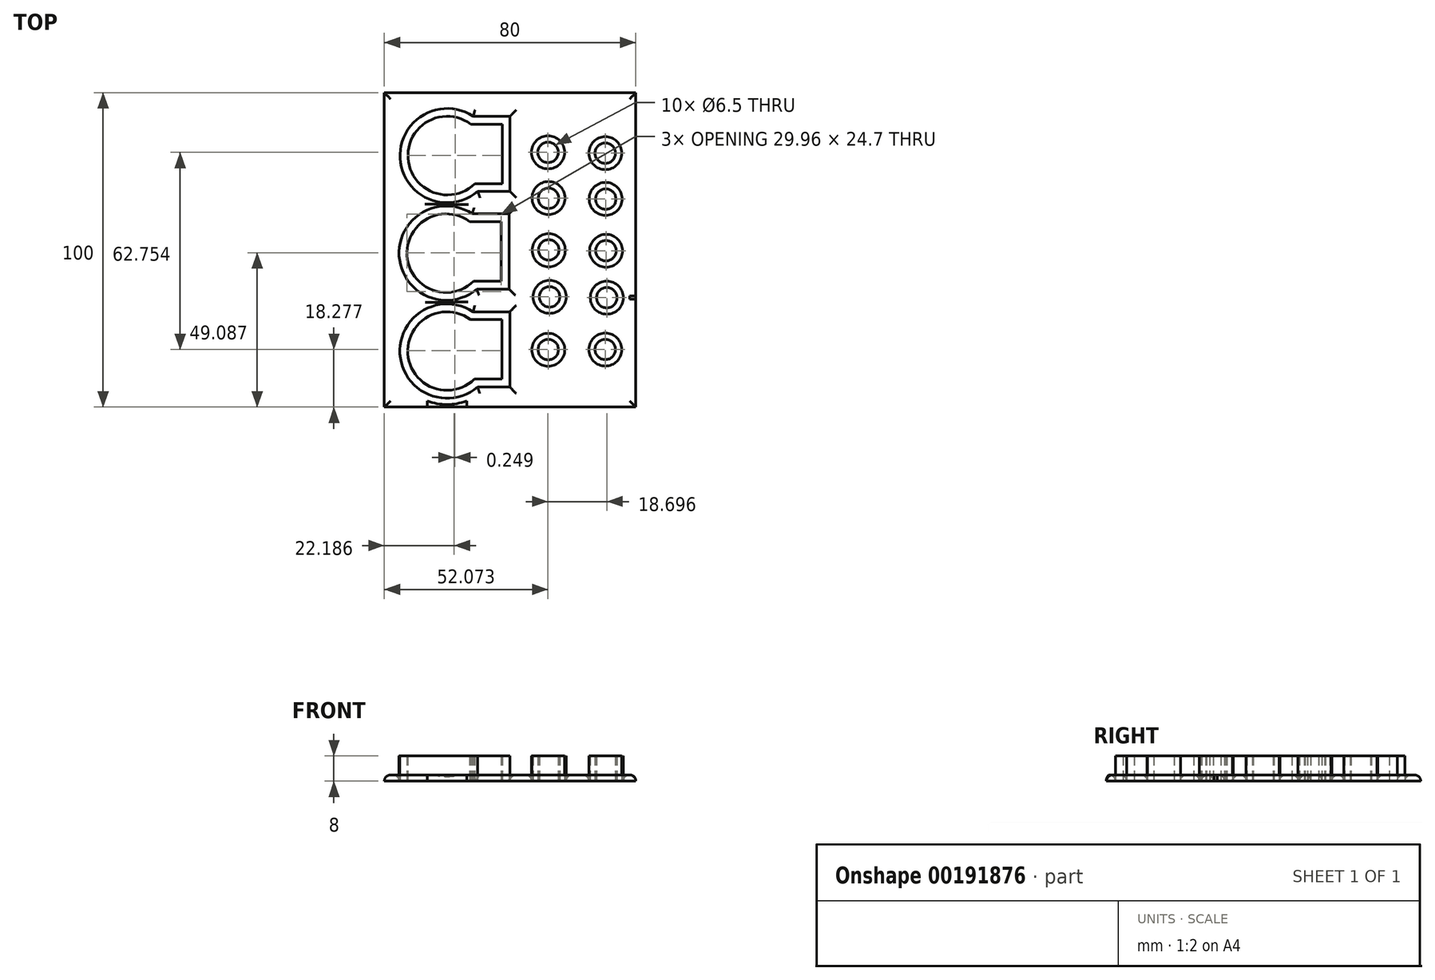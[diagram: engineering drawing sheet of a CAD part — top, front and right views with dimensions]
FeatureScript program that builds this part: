
annotation { "Feature Type Name" : "Feature", "Feature Type Description" : "" }
export const myFeature = defineFeature(function(context is Context, id is Id, definition is map)
    precondition{}
    {
        {
            var Q0;
            Q0=qCreatedBy(makeId("Top.planeOp"),FACE);
            var sketch = newSketch(context, id + "F0", { "sketchPlane" : qUnion([Q0])});
            skLineSegment(sketch, "E0.bottom", {"start": v(40, -50) * mm, "end": v(-40, -50) * mm});
            skLineSegment(sketch, "E0.top", {"start": v(40, 50) * mm, "end": v(-40, 50) * mm});
            skLineSegment(sketch, "E0.left", {"start": v(40, -50) * mm, "end": v(40, 50) * mm});
            skLineSegment(sketch, "E0.right", {"start": v(-40, -50) * mm, "end": v(-40, 50) * mm});
            skPoint(sketch, "E0.middle", {"position": v(0, 0) * mm});
            skArc(sketch, "E1", {"start": v(-12.51, 40) * mm, "mid": v(-32.47, 29.17) * mm, "end": v(-11.25, 21.07) * mm});
            skLineSegment(sketch, "E2.bottom", {"start": v(-2.51, 21.07) * mm, "end": v(-11.25, 21.07) * mm});
            skLineSegment(sketch, "E2.top", {"start": v(-2.51, 40) * mm, "end": v(-12.51, 40) * mm});
            skLineSegment(sketch, "E2.left", {"start": v(-2.51, 21.07) * mm, "end": v(-2.51, 40) * mm});
            skPoint(sketch, "E2.middle", {"position": v(-7.51, 30.54) * mm});
            skLineSegment(sketch, "E3.trimOffspring", {"start": v(-12.51, 40) * mm, "end": v(-12.51, 40) * mm});
            skPoint(sketch, "E4.orphan", {"position": v(-40, 25) * mm});
            skPoint(sketch, "E5.middle", {"position": v(-7.56, -0.43) * mm});
            skPoint(sketch, "E6.middle", {"position": v(0.3, -31.2) * mm});
            skPoint(sketch, "E7.middle", {"position": v(-7.26, -31.66) * mm});
            skCircle(sketch, "E8", {"center": v(12.29, 0) * mm, "radius": 3.25 * mm});
            skCircle(sketch, "E9", {"center": v(30.5, -0.27) * mm, "radius": 3.25 * mm});
            skCircle(sketch, "E10", {"center": v(12.23, 16.42) * mm, "radius": 3.25 * mm});
            skCircle(sketch, "E11", {"center": v(30.43, 16.15) * mm, "radius": 3.25 * mm});
            skCircle(sketch, "E12", {"center": v(12.07, 31.03) * mm, "radius": 3.25 * mm});
            skCircle(sketch, "E13", {"center": v(30.28, 30.76) * mm, "radius": 3.25 * mm});
            skCircle(sketch, "E14", {"center": v(12.57, -14.93) * mm, "radius": 3.25 * mm});
            skCircle(sketch, "E15", {"center": v(30.77, -15.2) * mm, "radius": 3.25 * mm});
            skCircle(sketch, "E16", {"center": v(12.14, -31.72) * mm, "radius": 3.25 * mm});
            skCircle(sketch, "E17", {"center": v(30.29, -31.67) * mm, "radius": 3.25 * mm});
            skPoint(sketch, "E18.orphan", {"position": v(-12.51, 21.07) * mm});
            skPoint(sketch, "E19.orphan", {"position": v(-12.56, -10.43) * mm});
            skPoint(sketch, "E20.orphan", {"position": v(-12.26, -41.66) * mm});
            skArc(sketch, "E21.0", {"start": v(-11.72, 42.5) * mm, "mid": v(-34.97, 29.1) * mm, "end": v(-10.28, 18.57) * mm});
            skLineSegment(sketch, "E21.1", {"start": v(-0.01, 42.5) * mm, "end": v(-11.72, 42.5) * mm});
            skLineSegment(sketch, "E21.2", {"start": v(-0.01, 18.57) * mm, "end": v(-0.01, 42.5) * mm});
            skLineSegment(sketch, "E21.3", {"start": v(-0.01, 18.57) * mm, "end": v(-10.28, 18.57) * mm});
            skArc(sketch, "E22", {"start": v(-12.83, 8.98) * mm, "mid": v(-32.8, -1.86) * mm, "end": v(-11.57, -9.96) * mm});
            skLineSegment(sketch, "E23.bottom", {"start": v(-2.83, -9.96) * mm, "end": v(-11.57, -9.96) * mm});
            skLineSegment(sketch, "E23.top", {"start": v(-2.83, 8.98) * mm, "end": v(-12.83, 8.98) * mm});
            skLineSegment(sketch, "E23.left", {"start": v(-2.83, -9.96) * mm, "end": v(-2.83, 8.98) * mm});
            skPoint(sketch, "E23.middle", {"position": v(-7.83, -0.49) * mm});
            skLineSegment(sketch, "E24.trimOffspring", {"start": v(-12.83, 8.98) * mm, "end": v(-12.83, 8.98) * mm});
            skPoint(sketch, "E25.orphan", {"position": v(-12.83, -9.96) * mm});
            skArc(sketch, "E26.0", {"start": v(-12.04, 11.48) * mm, "mid": v(-35.3, -1.93) * mm, "end": v(-10.6, -12.46) * mm});
            skLineSegment(sketch, "E26.1", {"start": v(-0.33, 11.48) * mm, "end": v(-12.04, 11.48) * mm});
            skLineSegment(sketch, "E26.2", {"start": v(-0.33, -12.46) * mm, "end": v(-0.33, 11.48) * mm});
            skLineSegment(sketch, "E26.3", {"start": v(-0.33, -12.46) * mm, "end": v(-10.6, -12.46) * mm});
            skArc(sketch, "E27", {"start": v(-12.58, -22.18) * mm, "mid": v(-32.55, -33.02) * mm, "end": v(-11.32, -41.11) * mm});
            skLineSegment(sketch, "E28.bottom", {"start": v(-2.58, -41.11) * mm, "end": v(-11.32, -41.11) * mm});
            skLineSegment(sketch, "E28.top", {"start": v(-2.58, -22.18) * mm, "end": v(-12.58, -22.18) * mm});
            skLineSegment(sketch, "E28.left", {"start": v(-2.58, -41.11) * mm, "end": v(-2.58, -22.18) * mm});
            skPoint(sketch, "E28.middle", {"position": v(-7.58, -31.65) * mm});
            skLineSegment(sketch, "E29.trimOffspring", {"start": v(-12.58, -22.18) * mm, "end": v(-12.58, -22.18) * mm});
            skPoint(sketch, "E30.orphan", {"position": v(-12.58, -41.11) * mm});
            skArc(sketch, "E31.0", {"start": v(-11.8, -19.68) * mm, "mid": v(-35.05, -33.09) * mm, "end": v(-10.36, -43.61) * mm});
            skLineSegment(sketch, "E31.1", {"start": v(-0.08, -19.68) * mm, "end": v(-11.8, -19.68) * mm});
            skLineSegment(sketch, "E31.2", {"start": v(-0.08, -43.61) * mm, "end": v(-0.08, -19.68) * mm});
            skLineSegment(sketch, "E31.3", {"start": v(-0.08, -43.61) * mm, "end": v(-10.36, -43.61) * mm});
            skCircle(sketch, "E32.0", {"center": v(12.07, 31.03) * mm, "radius": 5.25 * mm});
            skCircle(sketch, "E33.0", {"center": v(30.3, 30.78) * mm, "radius": 5.25 * mm});
            skCircle(sketch, "E34.0", {"center": v(30.4, 16.22) * mm, "radius": 5.25 * mm});
            skCircle(sketch, "E35.0", {"center": v(12.23, 16.5) * mm, "radius": 5.25 * mm});
            skCircle(sketch, "E36.0", {"center": v(12.3, -0.11) * mm, "radius": 5.25 * mm});
            skCircle(sketch, "E37.0", {"center": v(30.55, -0.3) * mm, "radius": 5.25 * mm});
            skCircle(sketch, "E38.0", {"center": v(12.58, -14.95) * mm, "radius": 5.25 * mm});
            skCircle(sketch, "E39.0", {"center": v(30.77, -15.2) * mm, "radius": 5.25 * mm});
            skCircle(sketch, "E40.0", {"center": v(12.15, -31.78) * mm, "radius": 5.25 * mm});
            skCircle(sketch, "E41.0", {"center": v(30.3, -31.7) * mm, "radius": 5.25 * mm});
            skSolve(sketch);
        }
        {
            var Q0;
            Q0=makeQuery(id+"F0.imprint","IMPRINT",FACE,{"disambiguationData":[TD([[makeQuery(id+"F0.imprint","IMPRINT",EDGE,{"derivedFrom":sQuery(id+"F0.wireOp",EDGE,"E0.bottom")}),-1.0]])]});
            extrude(context, id + "F1", {"entities" : qUnion([Q0]), "depth" : 2 * mm});
        }
        {
            var Q0;
            Q0=makeQuery(id+"F0.imprint","IMPRINT",FACE,{"disambiguationData":[TD([[makeQuery(id+"F0.imprint","IMPRINT",EDGE,{"derivedFrom":sQuery(id+"F0.wireOp",EDGE,"E13")}),-1.0]])]});
            var Q1;
            Q1=makeQuery(id+"F0.imprint","IMPRINT",FACE,{"disambiguationData":[TD([[makeQuery(id+"F0.imprint","IMPRINT",EDGE,{"derivedFrom":sQuery(id+"F0.wireOp",EDGE,"E11")}),-1.0]])]});
            var Q2;
            Q2=makeQuery(id+"F0.imprint","IMPRINT",FACE,{"disambiguationData":[TD([[makeQuery(id+"F0.imprint","IMPRINT",EDGE,{"derivedFrom":sQuery(id+"F0.wireOp",EDGE,"E10")}),-1.0]])]});
            var Q3;
            Q3=makeQuery(id+"F0.imprint","IMPRINT",FACE,{"disambiguationData":[TD([[makeQuery(id+"F0.imprint","IMPRINT",EDGE,{"derivedFrom":sQuery(id+"F0.wireOp",EDGE,"E12")}),-1.0]])]});
            var Q4;
            Q4=makeQuery(id+"F0.imprint","IMPRINT",FACE,{"disambiguationData":[TD([[makeQuery(id+"F0.imprint","IMPRINT",EDGE,{"derivedFrom":sQuery(id+"F0.wireOp",EDGE,"E9")}),-1.0]])]});
            var Q5;
            Q5=makeQuery(id+"F0.imprint","IMPRINT",FACE,{"disambiguationData":[TD([[makeQuery(id+"F0.imprint","IMPRINT",EDGE,{"derivedFrom":sQuery(id+"F0.wireOp",EDGE,"E8")}),-1.0]])]});
            var Q6;
            Q6=makeQuery(id+"F0.imprint","IMPRINT",FACE,{"disambiguationData":[TD([[makeQuery(id+"F0.imprint","IMPRINT",EDGE,{"derivedFrom":sQuery(id+"F0.wireOp",EDGE,"E14")}),-1.0]])]});
            var Q7;
            Q7=makeQuery(id+"F0.imprint","IMPRINT",FACE,{"disambiguationData":[TD([[makeQuery(id+"F0.imprint","IMPRINT",EDGE,{"derivedFrom":sQuery(id+"F0.wireOp",EDGE,"E16")}),-1.0]])]});
            var Q8;
            Q8=makeQuery(id+"F0.imprint","IMPRINT",FACE,{"disambiguationData":[TD([[makeQuery(id+"F0.imprint","IMPRINT",EDGE,{"derivedFrom":sQuery(id+"F0.wireOp",EDGE,"E17")}),-1.0]])]});
            var Q9;
            Q9=makeQuery(id+"F0.imprint","IMPRINT",FACE,{"disambiguationData":[TD([[makeQuery(id+"F0.imprint","IMPRINT",EDGE,{"derivedFrom":sQuery(id+"F0.wireOp",EDGE,"E15")}),-1.0]])]});
            var Q10;
            Q10=makeQuery(id+"F0.imprint","IMPRINT",FACE,{"disambiguationData":[TD([[makeQuery(id+"F0.imprint","IMPRINT",EDGE,{"derivedFrom":sQuery(id+"F0.wireOp",EDGE,"E1")}),-1.0]])]});
            var Q11;
            Q11=makeQuery(id+"F0.imprint","IMPRINT",FACE,{"disambiguationData":[TD([[makeQuery(id+"F0.imprint","IMPRINT",EDGE,{"derivedFrom":sQuery(id+"F0.wireOp",EDGE,"E22")}),-1.0]])]});
            var Q12;
            Q12=makeQuery(id+"F0.imprint","IMPRINT",FACE,{"disambiguationData":[TD([[makeQuery(id+"F0.imprint","IMPRINT",EDGE,{"derivedFrom":sQuery(id+"F0.wireOp",EDGE,"E27")}),-1.0]])]});
            extrude(context, id + "F2", {"entities" : qUnion([Q0, Q1, Q2, Q3, Q4, Q5, Q6, Q7, Q8, Q9, Q10, Q11, Q12]), "depth" : 8 * mm});
        }
        {
            var Q0;
            Q0=makeQuery(id+"F1.opExtrude","CAP_EDGE",EDGE,{"disambiguationData":[OSD([sQuery(id+"F0.wireOp",EDGE,"E41.0")])],"isStart":false});
            var Q1;
            Q1=makeQuery(id+"F1.opExtrude","CAP_EDGE",EDGE,{"disambiguationData":[OSD([sQuery(id+"F0.wireOp",EDGE,"E39.0")])],"isStart":false});
            var Q2;
            Q2=makeQuery(id+"F1.opExtrude","CAP_EDGE",EDGE,{"disambiguationData":[OSD([sQuery(id+"F0.wireOp",EDGE,"E37.0")])],"isStart":false});
            var Q3;
            Q3=makeQuery(id+"F1.opExtrude","CAP_EDGE",EDGE,{"disambiguationData":[OSD([sQuery(id+"F0.wireOp",EDGE,"E34.0")])],"isStart":false});
            var Q4;
            Q4=makeQuery(id+"F1.opExtrude","CAP_EDGE",EDGE,{"disambiguationData":[OSD([sQuery(id+"F0.wireOp",EDGE,"E33.0")])],"isStart":false});
            var Q5;
            Q5=makeQuery(id+"F1.opExtrude","CAP_EDGE",EDGE,{"disambiguationData":[OSD([sQuery(id+"F0.wireOp",EDGE,"E32.0")])],"isStart":false});
            var Q6;
            Q6=makeQuery(id+"F1.opExtrude","CAP_EDGE",EDGE,{"disambiguationData":[OSD([sQuery(id+"F0.wireOp",EDGE,"E35.0")])],"isStart":false});
            var Q7;
            Q7=makeQuery(id+"F1.opExtrude","CAP_EDGE",EDGE,{"disambiguationData":[OSD([sQuery(id+"F0.wireOp",EDGE,"E36.0")])],"isStart":false});
            var Q8;
            Q8=makeQuery(id+"F1.opExtrude","CAP_EDGE",EDGE,{"disambiguationData":[OSD([sQuery(id+"F0.wireOp",EDGE,"E38.0")])],"isStart":false});
            var Q9;
            Q9=makeQuery(id+"F1.opExtrude","CAP_EDGE",EDGE,{"disambiguationData":[OSD([sQuery(id+"F0.wireOp",EDGE,"E40.0")])],"isStart":false});
            fillet(context, id + "F3", {"entities" : qUnion([Q0, Q1, Q2, Q3, Q4, Q5, Q6, Q7, Q8, Q9]), "radius" : 2 * mm, "tangentPropagation" : true, "allowEdgeOverflow" : false});
        }
        {
            var Q0;
            Q0=makeQuery(id+"F1.opExtrude","CAP_EDGE",EDGE,{"disambiguationData":[OSD([sQuery(id+"F0.wireOp",EDGE,"E21.0")])],"isStart":false});
            var Q1;
            Q1=makeQuery(id+"F1.opExtrude","CAP_EDGE",EDGE,{"disambiguationData":[OSD([sQuery(id+"F0.wireOp",EDGE,"E21.1")])],"isStart":false});
            var Q2;
            Q2=makeQuery(id+"F1.opExtrude","CAP_EDGE",EDGE,{"disambiguationData":[OSD([sQuery(id+"F0.wireOp",EDGE,"E26.0")])],"isStart":false});
            var Q3;
            Q3=makeQuery(id+"F1.opExtrude","CAP_EDGE",EDGE,{"disambiguationData":[OSD([sQuery(id+"F0.wireOp",EDGE,"E31.0")])],"isStart":false});
            var Q4;
            Q4=makeQuery(id+"F1.opExtrude","CAP_EDGE",EDGE,{"disambiguationData":[OSD([sQuery(id+"F0.wireOp",EDGE,"E21.2")])],"isStart":false});
            var Q5;
            Q5=makeQuery(id+"F1.opExtrude","CAP_EDGE",EDGE,{"disambiguationData":[OSD([sQuery(id+"F0.wireOp",EDGE,"E26.2")])],"isStart":false});
            var Q6;
            Q6=makeQuery(id+"F1.opExtrude","CAP_EDGE",EDGE,{"disambiguationData":[OSD([sQuery(id+"F0.wireOp",EDGE,"E21.3")])],"isStart":false});
            var Q7;
            Q7=makeQuery(id+"F1.opExtrude","CAP_EDGE",EDGE,{"disambiguationData":[OSD([sQuery(id+"F0.wireOp",EDGE,"E26.1")])],"isStart":false});
            var Q8;
            Q8=makeQuery(id+"F1.opExtrude","CAP_EDGE",EDGE,{"disambiguationData":[OSD([sQuery(id+"F0.wireOp",EDGE,"E31.1")])],"isStart":false});
            var Q9;
            Q9=makeQuery(id+"F1.opExtrude","CAP_EDGE",EDGE,{"disambiguationData":[OSD([sQuery(id+"F0.wireOp",EDGE,"E26.3")])],"isStart":false});
            var Q10;
            Q10=makeQuery(id+"F1.opExtrude","CAP_EDGE",EDGE,{"disambiguationData":[OSD([sQuery(id+"F0.wireOp",EDGE,"E31.3")])],"isStart":false});
            fillet(context, id + "F4", {"entities" : qUnion([Q0, Q1, Q2, Q3, Q4, Q5, Q6, Q7, Q8, Q9, Q10]), "radius" : 2 * mm, "tangentPropagation" : true, "allowEdgeOverflow" : false});
        }
        {
            var Q0;
            Q0=makeQuery(id+"F1.opExtrude","CAP_FACE",FACE,{"disambiguationData":[OSD([sQuery(id+"F0.wireOp",EDGE,"E0.bottom"),sQuery(id+"F0.wireOp",EDGE,"E0.top"),sQuery(id+"F0.wireOp",EDGE,"E0.left"),sQuery(id+"F0.wireOp",EDGE,"E0.right"),sQuery(id+"F0.wireOp",EDGE,"E21.0"),sQuery(id+"F0.wireOp",EDGE,"E21.1"),sQuery(id+"F0.wireOp",EDGE,"E21.2"),sQuery(id+"F0.wireOp",EDGE,"E21.3"),sQuery(id+"F0.wireOp",EDGE,"E26.0"),sQuery(id+"F0.wireOp",EDGE,"E26.1"),sQuery(id+"F0.wireOp",EDGE,"E26.2"),sQuery(id+"F0.wireOp",EDGE,"E26.3"),sQuery(id+"F0.wireOp",EDGE,"E31.0"),sQuery(id+"F0.wireOp",EDGE,"E31.1"),sQuery(id+"F0.wireOp",EDGE,"E31.2"),sQuery(id+"F0.wireOp",EDGE,"E31.3"),sQuery(id+"F0.wireOp",EDGE,"E32.0"),sQuery(id+"F0.wireOp",EDGE,"E33.0"),sQuery(id+"F0.wireOp",EDGE,"E34.0"),sQuery(id+"F0.wireOp",EDGE,"E35.0"),sQuery(id+"F0.wireOp",EDGE,"E36.0"),sQuery(id+"F0.wireOp",EDGE,"E37.0"),sQuery(id+"F0.wireOp",EDGE,"E38.0"),sQuery(id+"F0.wireOp",EDGE,"E39.0"),sQuery(id+"F0.wireOp",EDGE,"E40.0"),sQuery(id+"F0.wireOp",EDGE,"E41.0")])],"isStart":false});
            fillet(context, id + "F5", {"entities" : qUnion([Q0]), "radius" : 2 * mm, "tangentPropagation" : true, "allowEdgeOverflow" : false});
        }
    });
